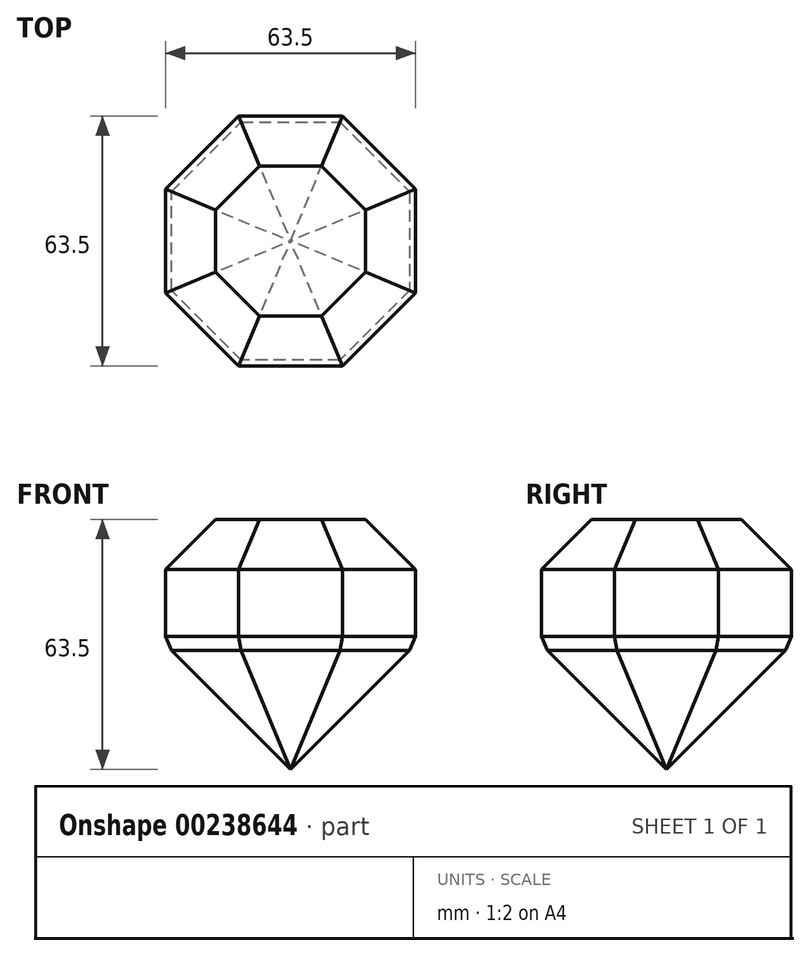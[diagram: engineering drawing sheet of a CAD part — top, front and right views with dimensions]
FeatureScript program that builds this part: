
annotation { "Feature Type Name" : "Feature", "Feature Type Description" : "" }
export const myFeature = defineFeature(function(context is Context, id is Id, definition is map)
    precondition{}
    {
        {
            var Q0;
            Q0=qCreatedBy(makeId("Top.planeOp"),FACE);
            var sketch = newSketch(context, id + "F0", { "sketchPlane" : qUnion([Q0])});
            skCircle(sketch, "E0.cCircle", {"center": v(0, 0) * mm, "radius": 31.75 * mm, "construction": true});
            skLineSegment(sketch, "E0.0", {"start": v(31.75, 13.15) * mm, "end": v(31.75, -13.15) * mm});
            skLineSegment(sketch, "E0.1", {"start": v(31.75, -13.15) * mm, "end": v(13.15, -31.75) * mm});
            skLineSegment(sketch, "E0.2", {"start": v(13.15, -31.75) * mm, "end": v(-13.15, -31.75) * mm});
            skLineSegment(sketch, "E0.3", {"start": v(-13.15, -31.75) * mm, "end": v(-31.75, -13.15) * mm});
            skLineSegment(sketch, "E0.4", {"start": v(-31.75, -13.15) * mm, "end": v(-31.75, 13.15) * mm});
            skLineSegment(sketch, "E0.5", {"start": v(-31.75, 13.15) * mm, "end": v(-13.15, 31.75) * mm});
            skLineSegment(sketch, "E0.6", {"start": v(-13.15, 31.75) * mm, "end": v(13.15, 31.75) * mm});
            skLineSegment(sketch, "E0.7", {"start": v(13.15, 31.75) * mm, "end": v(31.75, 13.15) * mm});
            skPoint(sketch, "E0.0.midPoint", {"position": v(31.75, 0) * mm});
            skSolve(sketch);
        }
        {
            var Q0;
            Q0=makeQuery(id+"F0.imprint","IMPRINT",FACE,{"disambiguationData":[TD([[makeQuery(id+"F0.imprint","IMPRINT",EDGE,{"derivedFrom":sQuery(id+"F0.wireOp",EDGE,"E0.0")}),-1.0]])]});
            extrude(context, id + "F1", {"entities" : qUnion([Q0]), "depth" : 25.4 * mm});
        }
        {
            var Q0;
            Q0=makeQuery(id+"F1.opExtrude","CAP_EDGE",EDGE,{"disambiguationData":[OSD([sQuery(id+"F0.wireOp",EDGE,"E0.4")])],"isStart":false});
            var Q1;
            Q1=makeQuery(id+"F1.opExtrude","CAP_EDGE",EDGE,{"disambiguationData":[OSD([sQuery(id+"F0.wireOp",EDGE,"E0.3")])],"isStart":false});
            var Q2;
            Q2=makeQuery(id+"F1.opExtrude","CAP_EDGE",EDGE,{"disambiguationData":[OSD([sQuery(id+"F0.wireOp",EDGE,"E0.2")])],"isStart":false});
            var Q3;
            Q3=makeQuery(id+"F1.opExtrude","CAP_EDGE",EDGE,{"disambiguationData":[OSD([sQuery(id+"F0.wireOp",EDGE,"E0.1")])],"isStart":false});
            var Q4;
            Q4=makeQuery(id+"F1.opExtrude","CAP_EDGE",EDGE,{"disambiguationData":[OSD([sQuery(id+"F0.wireOp",EDGE,"E0.0")])],"isStart":false});
            var Q5;
            Q5=makeQuery(id+"F1.opExtrude","CAP_EDGE",EDGE,{"disambiguationData":[OSD([sQuery(id+"F0.wireOp",EDGE,"E0.7")])],"isStart":false});
            var Q6;
            Q6=makeQuery(id+"F1.opExtrude","CAP_EDGE",EDGE,{"disambiguationData":[OSD([sQuery(id+"F0.wireOp",EDGE,"E0.6")])],"isStart":false});
            var Q7;
            Q7=makeQuery(id+"F1.opExtrude","CAP_EDGE",EDGE,{"disambiguationData":[OSD([sQuery(id+"F0.wireOp",EDGE,"E0.5")])],"isStart":false});
            chamfer(context, id + "F2", {"entities" : qUnion([Q0, Q1, Q2, Q3, Q4, Q5, Q6, Q7]), "width" : 12.7 * mm, "tangentPropagation" : true});
        }
        {
            var Q0;
            Q0=makeQuery(id+"F1.opExtrude","CAP_FACE",FACE,{"disambiguationData":[OSD([sQuery(id+"F0.wireOp",EDGE,"E0.0"),sQuery(id+"F0.wireOp",EDGE,"E0.1"),sQuery(id+"F0.wireOp",EDGE,"E0.2"),sQuery(id+"F0.wireOp",EDGE,"E0.3"),sQuery(id+"F0.wireOp",EDGE,"E0.4"),sQuery(id+"F0.wireOp",EDGE,"E0.5"),sQuery(id+"F0.wireOp",EDGE,"E0.6"),sQuery(id+"F0.wireOp",EDGE,"E0.7")])],"isStart":true});
            extrude(context, id + "F3", {"entities" : qUnion([Q0]), "operationType" : NewBodyOperationType.ADD, "depth" : 38.1 * mm});
        }
        {
            var Q0;
            Q0=makeQuery(id+"F3.opExtrude","CAP_EDGE",EDGE,{"disambiguationData":[OSD([sQuery(id+"F0.wireOp",EDGE,"E0.3")])],"isStart":false});
            var Q1;
            Q1=makeQuery(id+"F3.opExtrude","CAP_EDGE",EDGE,{"disambiguationData":[OSD([sQuery(id+"F0.wireOp",EDGE,"E0.2")])],"isStart":false});
            var Q2;
            Q2=makeQuery(id+"F3.opExtrude","CAP_EDGE",EDGE,{"disambiguationData":[OSD([sQuery(id+"F0.wireOp",EDGE,"E0.1")])],"isStart":false});
            var Q3;
            Q3=makeQuery(id+"F3.opExtrude","CAP_EDGE",EDGE,{"disambiguationData":[OSD([sQuery(id+"F0.wireOp",EDGE,"E0.4")])],"isStart":false});
            var Q4;
            Q4=makeQuery(id+"F3.opExtrude","CAP_EDGE",EDGE,{"disambiguationData":[OSD([sQuery(id+"F0.wireOp",EDGE,"E0.5")])],"isStart":false});
            var Q5;
            Q5=makeQuery(id+"F3.opExtrude","CAP_EDGE",EDGE,{"disambiguationData":[OSD([sQuery(id+"F0.wireOp",EDGE,"E0.6")])],"isStart":false});
            var Q6;
            Q6=makeQuery(id+"F3.opExtrude","CAP_EDGE",EDGE,{"disambiguationData":[OSD([sQuery(id+"F0.wireOp",EDGE,"E0.7")])],"isStart":false});
            var Q7;
            Q7=makeQuery(id+"F3.opExtrude","CAP_EDGE",EDGE,{"disambiguationData":[OSD([sQuery(id+"F0.wireOp",EDGE,"E0.0")])],"isStart":false});
            chamfer(context, id + "F4", {"entities" : qUnion([Q0, Q1, Q2, Q3, Q4, Q5, Q6, Q7]), "width" : 31.75 * mm, "tangentPropagation" : true});
        }
        {
            var Q0;
            {var subQ0=sQuery(id+"F0.wireOp",EDGE,"E0.4");Q0=makeQuery(id+"F4.opChamfer","BLEND_EDGE",EDGE,{"blendedFrom":[makeQuery(id+"F3.opExtrude","CAP_EDGE",EDGE,{"disambiguationData":[OSD([subQ0])],"isStart":false}),makeQuery(id+"F3.boolean.opBoolean","MERGE",FACE,{"derivedFrom":[makeQuery(id+"F1.opExtrude","SWEPT_FACE",FACE,{"disambiguationData":[OSD([subQ0])]}),makeQuery(id+"F3.opExtrude","SWEPT_FACE",FACE,{"disambiguationData":[OSD([subQ0])]})]})],"blendedInto":[makeQuery(id+"F3.boolean.opBoolean","MERGE",FACE,{"derivedFrom":[makeQuery(id+"F1.opExtrude","SWEPT_FACE",FACE,{"disambiguationData":[OSD([subQ0])]}),makeQuery(id+"F3.opExtrude","SWEPT_FACE",FACE,{"disambiguationData":[OSD([subQ0])]})]})]});}
            var Q1;
            {var subQ0=sQuery(id+"F0.wireOp",EDGE,"E0.5");Q1=makeQuery(id+"F4.opChamfer","BLEND_EDGE",EDGE,{"blendedFrom":[makeQuery(id+"F3.opExtrude","CAP_EDGE",EDGE,{"disambiguationData":[OSD([subQ0])],"isStart":false}),makeQuery(id+"F3.boolean.opBoolean","MERGE",FACE,{"derivedFrom":[makeQuery(id+"F1.opExtrude","SWEPT_FACE",FACE,{"disambiguationData":[OSD([subQ0])]}),makeQuery(id+"F3.opExtrude","SWEPT_FACE",FACE,{"disambiguationData":[OSD([subQ0])]})]})],"blendedInto":[makeQuery(id+"F3.boolean.opBoolean","MERGE",FACE,{"derivedFrom":[makeQuery(id+"F1.opExtrude","SWEPT_FACE",FACE,{"disambiguationData":[OSD([subQ0])]}),makeQuery(id+"F3.opExtrude","SWEPT_FACE",FACE,{"disambiguationData":[OSD([subQ0])]})]})]});}
            var Q2;
            {var subQ0=sQuery(id+"F0.wireOp",EDGE,"E0.3");Q2=makeQuery(id+"F4.opChamfer","BLEND_EDGE",EDGE,{"blendedFrom":[makeQuery(id+"F3.opExtrude","CAP_EDGE",EDGE,{"disambiguationData":[OSD([subQ0])],"isStart":false}),makeQuery(id+"F3.boolean.opBoolean","MERGE",FACE,{"derivedFrom":[makeQuery(id+"F1.opExtrude","SWEPT_FACE",FACE,{"disambiguationData":[OSD([subQ0])]}),makeQuery(id+"F3.opExtrude","SWEPT_FACE",FACE,{"disambiguationData":[OSD([subQ0])]})]})],"blendedInto":[makeQuery(id+"F3.boolean.opBoolean","MERGE",FACE,{"derivedFrom":[makeQuery(id+"F1.opExtrude","SWEPT_FACE",FACE,{"disambiguationData":[OSD([subQ0])]}),makeQuery(id+"F3.opExtrude","SWEPT_FACE",FACE,{"disambiguationData":[OSD([subQ0])]})]})]});}
            var Q3;
            {var subQ0=sQuery(id+"F0.wireOp",EDGE,"E0.2");Q3=makeQuery(id+"F4.opChamfer","BLEND_EDGE",EDGE,{"blendedFrom":[makeQuery(id+"F3.opExtrude","CAP_EDGE",EDGE,{"disambiguationData":[OSD([subQ0])],"isStart":false}),makeQuery(id+"F3.boolean.opBoolean","MERGE",FACE,{"derivedFrom":[makeQuery(id+"F1.opExtrude","SWEPT_FACE",FACE,{"disambiguationData":[OSD([subQ0])]}),makeQuery(id+"F3.opExtrude","SWEPT_FACE",FACE,{"disambiguationData":[OSD([subQ0])]})]})],"blendedInto":[makeQuery(id+"F3.boolean.opBoolean","MERGE",FACE,{"derivedFrom":[makeQuery(id+"F1.opExtrude","SWEPT_FACE",FACE,{"disambiguationData":[OSD([subQ0])]}),makeQuery(id+"F3.opExtrude","SWEPT_FACE",FACE,{"disambiguationData":[OSD([subQ0])]})]})]});}
            var Q4;
            {var subQ0=sQuery(id+"F0.wireOp",EDGE,"E0.1");Q4=makeQuery(id+"F4.opChamfer","BLEND_EDGE",EDGE,{"blendedFrom":[makeQuery(id+"F3.opExtrude","CAP_EDGE",EDGE,{"disambiguationData":[OSD([subQ0])],"isStart":false}),makeQuery(id+"F3.boolean.opBoolean","MERGE",FACE,{"derivedFrom":[makeQuery(id+"F1.opExtrude","SWEPT_FACE",FACE,{"disambiguationData":[OSD([subQ0])]}),makeQuery(id+"F3.opExtrude","SWEPT_FACE",FACE,{"disambiguationData":[OSD([subQ0])]})]})],"blendedInto":[makeQuery(id+"F3.boolean.opBoolean","MERGE",FACE,{"derivedFrom":[makeQuery(id+"F1.opExtrude","SWEPT_FACE",FACE,{"disambiguationData":[OSD([subQ0])]}),makeQuery(id+"F3.opExtrude","SWEPT_FACE",FACE,{"disambiguationData":[OSD([subQ0])]})]})]});}
            var Q5;
            {var subQ0=sQuery(id+"F0.wireOp",EDGE,"E0.0");Q5=makeQuery(id+"F4.opChamfer","BLEND_EDGE",EDGE,{"blendedFrom":[makeQuery(id+"F3.opExtrude","CAP_EDGE",EDGE,{"disambiguationData":[OSD([subQ0])],"isStart":false}),makeQuery(id+"F3.boolean.opBoolean","MERGE",FACE,{"derivedFrom":[makeQuery(id+"F1.opExtrude","SWEPT_FACE",FACE,{"disambiguationData":[OSD([subQ0])]}),makeQuery(id+"F3.opExtrude","SWEPT_FACE",FACE,{"disambiguationData":[OSD([subQ0])]})]})],"blendedInto":[makeQuery(id+"F3.boolean.opBoolean","MERGE",FACE,{"derivedFrom":[makeQuery(id+"F1.opExtrude","SWEPT_FACE",FACE,{"disambiguationData":[OSD([subQ0])]}),makeQuery(id+"F3.opExtrude","SWEPT_FACE",FACE,{"disambiguationData":[OSD([subQ0])]})]})]});}
            var Q6;
            {var subQ0=sQuery(id+"F0.wireOp",EDGE,"E0.7");Q6=makeQuery(id+"F4.opChamfer","BLEND_EDGE",EDGE,{"blendedFrom":[makeQuery(id+"F3.opExtrude","CAP_EDGE",EDGE,{"disambiguationData":[OSD([subQ0])],"isStart":false}),makeQuery(id+"F3.boolean.opBoolean","MERGE",FACE,{"derivedFrom":[makeQuery(id+"F1.opExtrude","SWEPT_FACE",FACE,{"disambiguationData":[OSD([subQ0])]}),makeQuery(id+"F3.opExtrude","SWEPT_FACE",FACE,{"disambiguationData":[OSD([subQ0])]})]})],"blendedInto":[makeQuery(id+"F3.boolean.opBoolean","MERGE",FACE,{"derivedFrom":[makeQuery(id+"F1.opExtrude","SWEPT_FACE",FACE,{"disambiguationData":[OSD([subQ0])]}),makeQuery(id+"F3.opExtrude","SWEPT_FACE",FACE,{"disambiguationData":[OSD([subQ0])]})]})]});}
            var Q7;
            {var subQ0=sQuery(id+"F0.wireOp",EDGE,"E0.6");Q7=makeQuery(id+"F4.opChamfer","BLEND_EDGE",EDGE,{"blendedFrom":[makeQuery(id+"F3.opExtrude","CAP_EDGE",EDGE,{"disambiguationData":[OSD([subQ0])],"isStart":false}),makeQuery(id+"F3.boolean.opBoolean","MERGE",FACE,{"derivedFrom":[makeQuery(id+"F1.opExtrude","SWEPT_FACE",FACE,{"disambiguationData":[OSD([subQ0])]}),makeQuery(id+"F3.opExtrude","SWEPT_FACE",FACE,{"disambiguationData":[OSD([subQ0])]})]})],"blendedInto":[makeQuery(id+"F3.boolean.opBoolean","MERGE",FACE,{"derivedFrom":[makeQuery(id+"F1.opExtrude","SWEPT_FACE",FACE,{"disambiguationData":[OSD([subQ0])]}),makeQuery(id+"F3.opExtrude","SWEPT_FACE",FACE,{"disambiguationData":[OSD([subQ0])]})]})]});}
            chamfer(context, id + "F5", {"entities" : qUnion([Q0, Q1, Q2, Q3, Q4, Q5, Q6, Q7]), "width" : 5.08 * mm, "tangentPropagation" : true});
        }
    });
